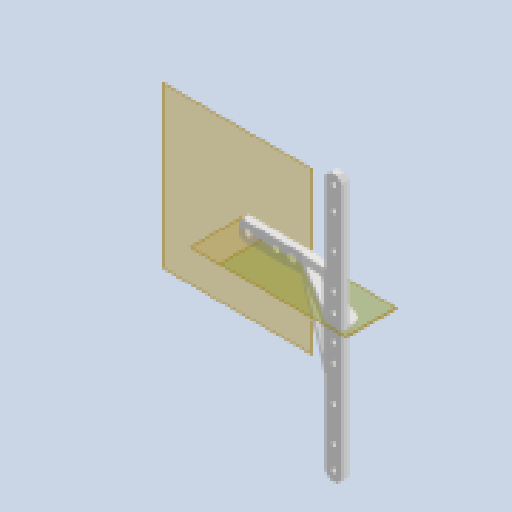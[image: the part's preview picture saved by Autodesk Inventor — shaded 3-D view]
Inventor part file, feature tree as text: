
AUTODESK INVENTOR PART (.ipt)
format: ipt  version: 2023 (Build 270158000, 158)  size: 371,712 bytes
history: native  units: mm
features: other x12, sketch x10, extrude x9, reference x8, projected_geometry x8, thicken_offset x5, plane x4, fillet x4, chamfer x4, loft x1, mirror x1
ambient origin geometry x8: Origin, YZ Plane, XZ Plane, XY Plane, X Axis, Y Axis, Z Axis, Center Point
bodies: Solid1 (feature_tree)
feature tree (66):
  extrude  "Extrusion1"  Depth=7.0mm
  plane  "Work Plane1"
  plane  "Work Plane2"
  extrude  "Extrusion2"  Depth=2.0mm
  sketch  "Sketch3"  dims[d4=2.0mm d5=2.0mm]
  loft  "Loft1"
  plane  "Work Plane3"
  extrude  "Extrusion3"  Depth=8.0mm
  fillet  "Fillet1"  Radius=15.0mm
  extrude  "Extrusion4"  Depth=2.0mm
  fillet  "Fillet2"  Radius=3.0mm
  fillet  "Fillet3"  Radius=3.0mm
  chamfer  "Chamfer1"  Angle=90.0deg  [1 undecoded]
  chamfer  "Chamfer2"  Angle=90.0deg  [1 undecoded]
  extrude  "Extrusion5"  Depth=2.0mm TaperAngle=0.0deg
  fillet  "Fillet4"  Radius=3.0mm
  thicken_offset  "Thicken1"
  thicken_offset  "Thicken2"
  extrude  "Extrusion6"  Depth=2.0mm
  chamfer  "Chamfer3"  Distance=4.0mm
  extrude  "Extrusion7"  Depth=4.0mm
  extrude  "Extrusion8"  Depth=2.0mm
  extrude  "Extrusion9"  Depth=2.0mm
  plane  "Work Plane4"
  mirror  "Mirror1"
  thicken_offset  "Thicken3"
  thicken_offset  "Thicken4"
  thicken_offset  "Thicken5"
  chamfer  "Chamfer5"  Distance=3.0mm
  sketch  "Sketch1"  dims[d0=7.0mm d1=87.0mm]
  reference  "Reference1"
  reference  "Reference2"
  sketch  "Sketch2"  dims[d2=2.0mm d3=2.0mm]
  reference  "Reference3"
  projected_geometry  "Projected Loop1"
  other  "Edges1"
  sketch  "Sketch5"  dims[d6=3.0mm d7=0.0mm d8=8.0mm d9=15.0mm]
  projected_geometry  "Projected Loop3"
  projected_geometry  "Projected Loop4"
  sketch  "Sketch6"  dims[d10=2.0mm d11=2.0mm d12=3.0mm d13=0.0mm d14=3.0mm]
  projected_geometry  "Projected Loop5"
  projected_geometry  "Projected Loop6"
  sketch  "Sketch7"  dims[d15=20.0mm]
  projected_geometry  "Projected Loop7"
  projected_geometry  "Projected Loop8"
  sketch  "Sketch8"  dims[d16=3.0mm]
  projected_geometry  "Projected Loop9"
  reference  "Reference4"
  sketch  "Sketch9"  dims[d17=20.0mm d18=0.0mm d19=90.0deg d20=0.0mm d21=90.0deg]
  reference  "Reference5"
  reference  "Reference6"
  sketch  "Sketch10"  dims[d22=5.0mm d23=2.0mm d24=0.0mm d25=3.0mm]
  reference  "Reference7"
  reference  "Reference8"
  sketch  "Sketch11"  dims[d26=2.0mm d27=2.0mm d28=4.0mm d29=4.0mm d30=2.0mm d31=2.0mm d32=3.0mm d33=0.0mm d34=0.5mm d35=1.0mm d36=1.5mm d37=3.0mm d38=2.0mm d39=2.0mm d40=45.0deg d41=2.0mm d42=2.0mm d43=45.0deg d44=15.0mm d45=8.0mm d46=15.0mm d47=8.0mm d48=2.0mm d49=2.0mm d50=2.0mm d51=2.0mm d52=3.0mm d53=0.0mm d54=1.0mm d55=0.5mm d56=0.5mm d57=0.5mm d58=0.5mm d59=14.0mm d60=8.0mm d61=3.0mm d62=0.0mm d63=1.5mm d64=2.0mm d65=45.0deg d66=7.0mm d67=16.0mm d68=3.0mm d69=0.0mm d70=2.0mm d71=2.0mm d72=3.0mm d73=0.0mm d74=3.0mm d75=0.0mm d79=1.0mm d80=1.0mm d81=1.0mm d82=1.0mm d83=1.0mm d84=1.0mm d85=2.0mm d86=2.0mm d87=45.0deg]
  parser-record x2  (decoder bookkeeping rows leaked as tree rows — omitted from the tree; the rows remain in map.json)
  other  "body_8d_1.iam"
  other  "leg_2d_1:2"
  other  "leg_holder_2:1"
  other  "leg_1_2d_MIR:2"
  other  "leg_holder_2_MIR:1"
  other  "body_linker_1_8d:1"
  other  "body_8d_wid_1.iam"
  other  "body_linker_1_wid_8d:1"
  other  "leg_2d_1:1"
note: 2 required parameter values undecoded (feature->parameter linkage not recoverable at this tier; creation-order binding heuristic only, values carry confidence <= 0.55)
note: 2 file-system paths scrubbed to <path> (originals preserved in map.json)
